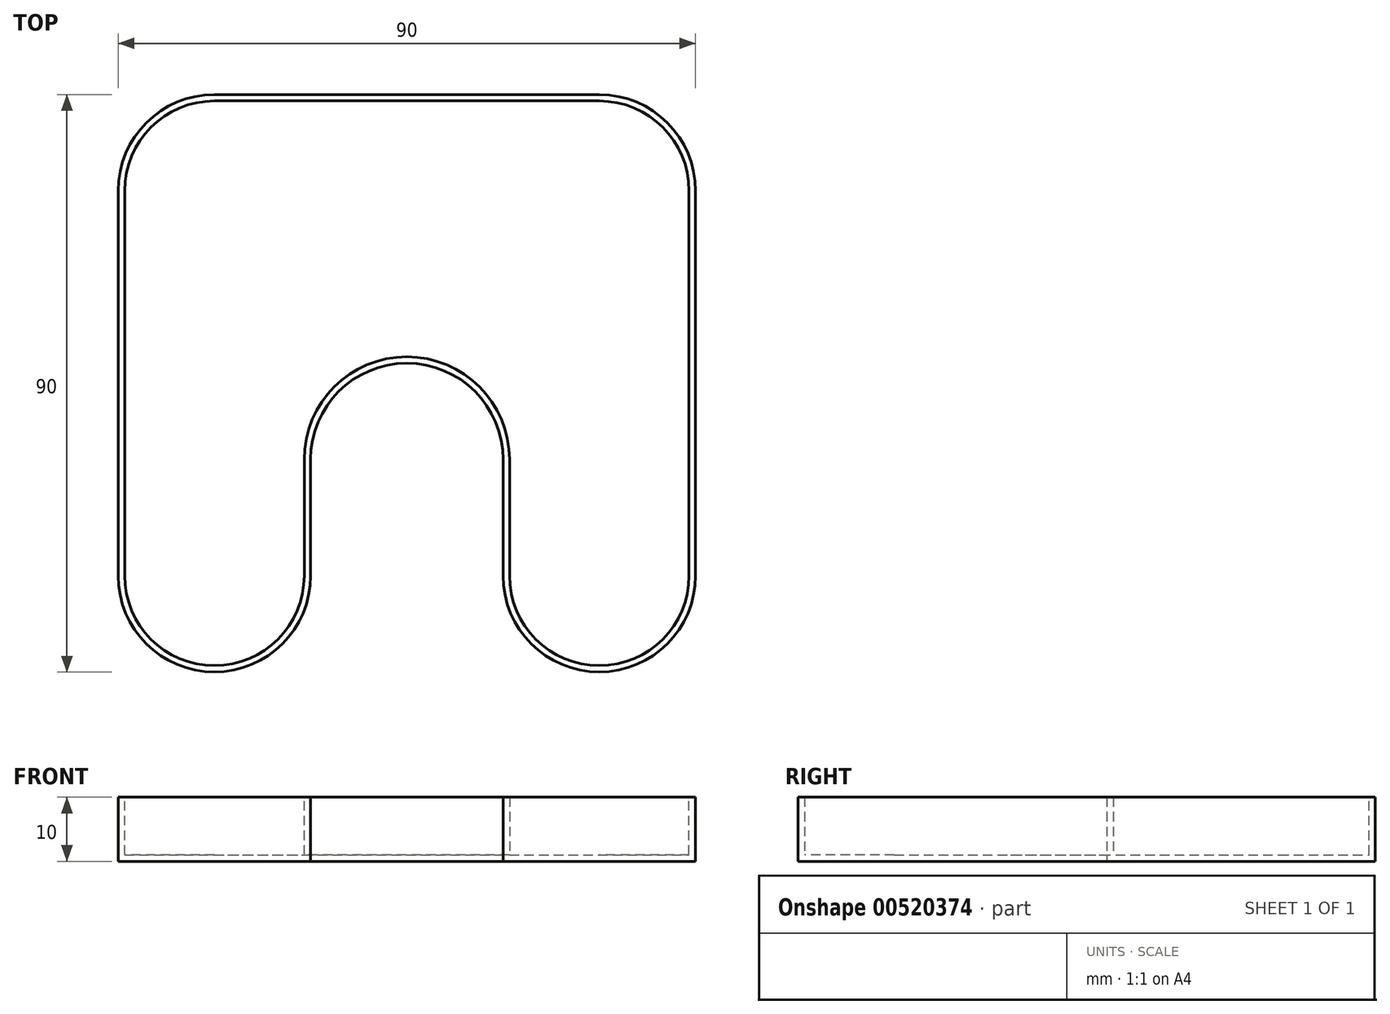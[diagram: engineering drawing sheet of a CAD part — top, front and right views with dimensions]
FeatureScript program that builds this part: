
annotation { "Feature Type Name" : "Feature", "Feature Type Description" : "" }
export const myFeature = defineFeature(function(context is Context, id is Id, definition is map)
    precondition{}
    {
        {
            var Q0;
            Q0=qCreatedBy(makeId("Top.planeOp"),FACE);
            var sketch = newSketch(context, id + "F0", { "sketchPlane" : qUnion([Q0])});
            skLineSegment(sketch, "E0.bottom", {"start": v(15, 0) * mm, "end": v(15, 0) * mm});
            skLineSegment(sketch, "E0.top", {"start": v(15, 90) * mm, "end": v(75, 90) * mm});
            skLineSegment(sketch, "E0.left", {"start": v(0, 15) * mm, "end": v(0, 75) * mm});
            skLineSegment(sketch, "E0.right", {"start": v(90, 15) * mm, "end": v(90, 75) * mm});
            skLineSegment(sketch, "E1", {"start": v(30, 15) * mm, "end": v(30, 33.13) * mm});
            skLineSegment(sketch, "E2", {"start": v(45, 48.13) * mm, "end": v(45, 48.13) * mm});
            skLineSegment(sketch, "E3", {"start": v(60, 33.13) * mm, "end": v(60, 15) * mm});
            skLineSegment(sketch, "E4.trimOffspring", {"start": v(75, 0) * mm, "end": v(75, 0) * mm});
            skPoint(sketch, "E5.visualSharp", {"position": v(0, 90) * mm});
            skArc(sketch, "E5.filletArc", {"start": v(15, 90) * mm, "mid": v(4.4, 85.6) * mm, "end": v(0, 75) * mm});
            skPoint(sketch, "E6.visualSharp", {"position": v(90, 90) * mm});
            skArc(sketch, "E6.filletArc", {"start": v(90, 75) * mm, "mid": v(85.6, 85.6) * mm, "end": v(75, 90) * mm});
            skPoint(sketch, "E7.visualSharp", {"position": v(30, 48.13) * mm});
            skArc(sketch, "E7.filletArc", {"start": v(45, 48.13) * mm, "mid": v(34.4, 43.74) * mm, "end": v(30, 33.13) * mm});
            skPoint(sketch, "E8.visualSharp", {"position": v(60, 48.13) * mm});
            skArc(sketch, "E8.filletArc", {"start": v(60, 33.13) * mm, "mid": v(55.6, 43.74) * mm, "end": v(45, 48.13) * mm});
            skPoint(sketch, "E9.visualSharp", {"position": v(0, 0) * mm});
            skArc(sketch, "E9.filletArc", {"start": v(0, 15) * mm, "mid": v(4.4, 4.4) * mm, "end": v(15, 0) * mm});
            skPoint(sketch, "E10.visualSharp", {"position": v(30, 0) * mm});
            skArc(sketch, "E10.filletArc", {"start": v(15, 0) * mm, "mid": v(25.6, 4.4) * mm, "end": v(30, 15) * mm});
            skPoint(sketch, "E11.visualSharp", {"position": v(60, 0) * mm});
            skArc(sketch, "E11.filletArc", {"start": v(60, 15) * mm, "mid": v(64.4, 4.4) * mm, "end": v(75, 0) * mm});
            skPoint(sketch, "E12.visualSharp", {"position": v(90, 0) * mm});
            skArc(sketch, "E12.filletArc", {"start": v(75, 0) * mm, "mid": v(85.6, 4.4) * mm, "end": v(90, 15) * mm});
            skSolve(sketch);
        }
        {
            var Q0;
            Q0=makeQuery(id+"F0.imprint","IMPRINT",FACE,{"disambiguationData":[TD([[makeQuery(id+"F0.imprint","IMPRINT",EDGE,{"derivedFrom":sQuery(id+"F0.wireOp",EDGE,"E0.top")}),-1.0]])]});
            extrude(context, id + "F1", {"entities" : qUnion([Q0]), "depth" : 10 * mm, "offsetDistance" : 25 * mm});
        }
        {
            var Q0;
            Q0=makeQuery(id+"F1.opExtrude","CAP_FACE",FACE,{"disambiguationData":[OSD([sQuery(id+"F0.wireOp",EDGE,"E0.top"),sQuery(id+"F0.wireOp",EDGE,"E0.left"),sQuery(id+"F0.wireOp",EDGE,"E0.right"),sQuery(id+"F0.wireOp",EDGE,"E1"),sQuery(id+"F0.wireOp",EDGE,"E3"),sQuery(id+"F0.wireOp",EDGE,"E5.filletArc"),sQuery(id+"F0.wireOp",EDGE,"E6.filletArc"),sQuery(id+"F0.wireOp",EDGE,"E7.filletArc"),sQuery(id+"F0.wireOp",EDGE,"E8.filletArc"),sQuery(id+"F0.wireOp",EDGE,"E9.filletArc"),sQuery(id+"F0.wireOp",EDGE,"E10.filletArc"),sQuery(id+"F0.wireOp",EDGE,"E11.filletArc"),sQuery(id+"F0.wireOp",EDGE,"E12.filletArc")])],"isStart":false});
            shell(context, id + "F2", {"entities" : qUnion([Q0]), "thickness" : 1 * mm});
        }
    });
